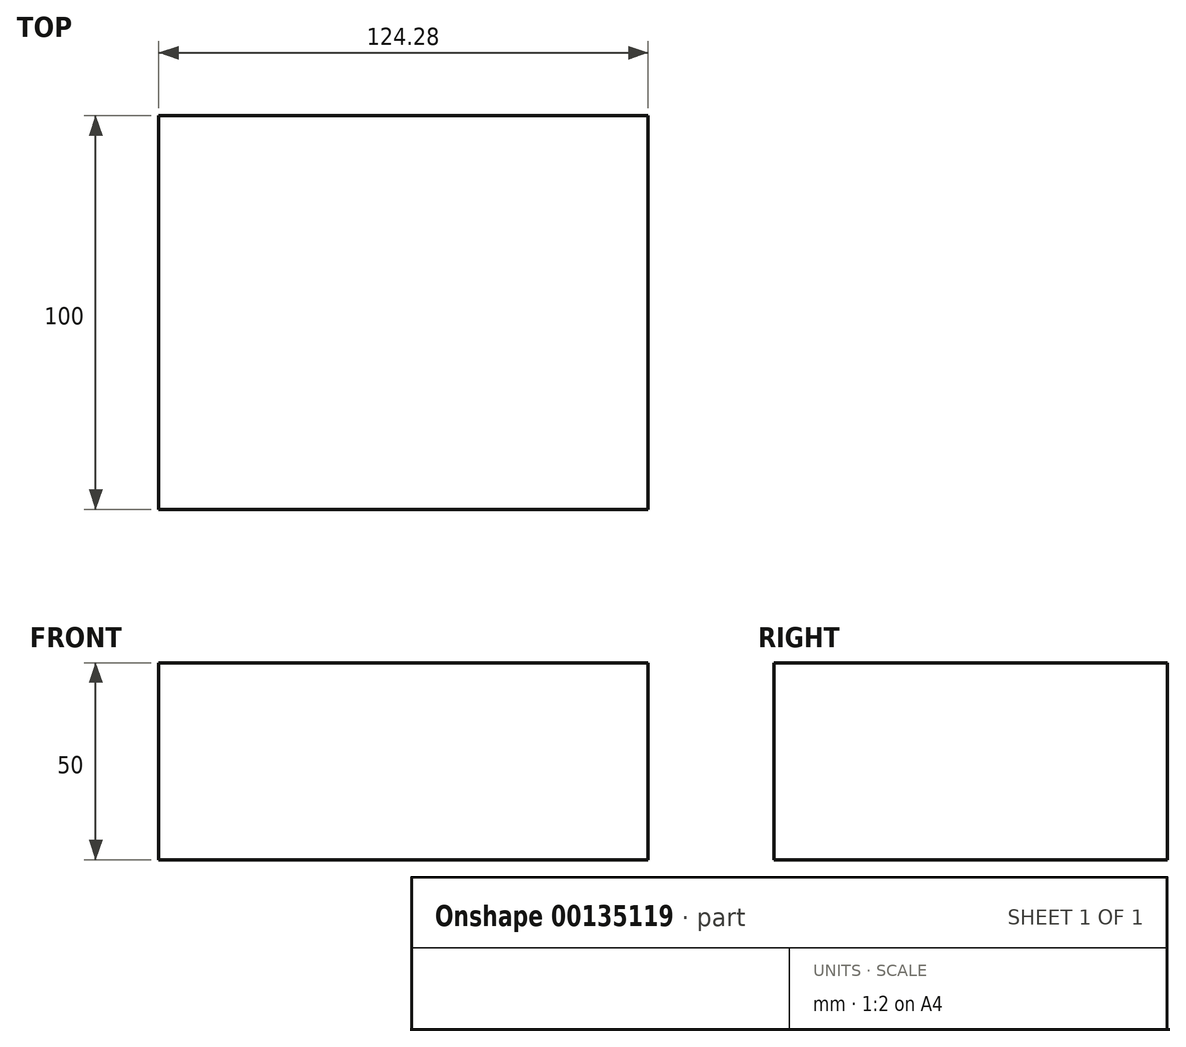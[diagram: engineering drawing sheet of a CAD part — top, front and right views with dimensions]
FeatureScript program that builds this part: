
annotation { "Feature Type Name" : "Feature", "Feature Type Description" : "" }
export const myFeature = defineFeature(function(context is Context, id is Id, definition is map)
    precondition{}
    {
        {
            var Q0;
            Q0=qCreatedBy(makeId("Top.planeOp"),FACE);
            var sketch = newSketch(context, id + "F0", { "sketchPlane" : qUnion([Q0])});
            skLineSegment(sketch, "E0.bottom", {"start": v(-62.14, 52.12) * mm, "end": v(62.14, 52.12) * mm});
            skLineSegment(sketch, "E0.top", {"start": v(-62.14, -47.88) * mm, "end": v(62.14, -47.88) * mm});
            skLineSegment(sketch, "E0.left", {"start": v(-62.14, 52.12) * mm, "end": v(-62.14, -47.88) * mm});
            skLineSegment(sketch, "E0.right", {"start": v(62.14, 52.12) * mm, "end": v(62.14, -47.88) * mm});
            skSolve(sketch);
        }
        {
            var Q0;
            Q0 = qSketchRegion(id + "F0", true);
            extrude(context, id + "F1", {"entities" : qUnion([Q0]), "depth" : 50 * mm});
        }
    });
